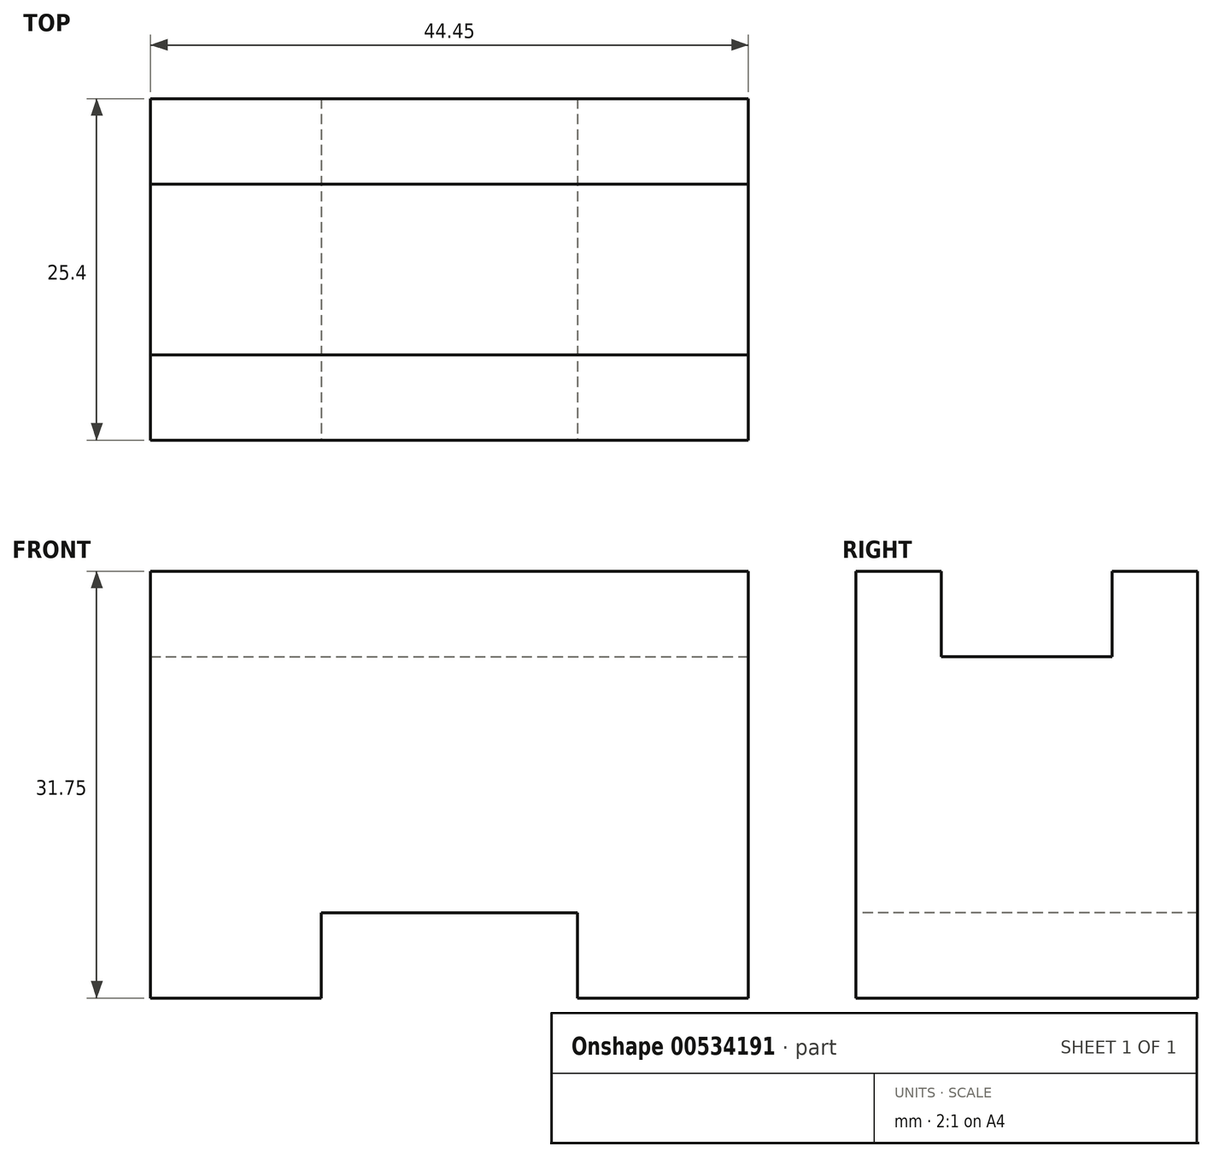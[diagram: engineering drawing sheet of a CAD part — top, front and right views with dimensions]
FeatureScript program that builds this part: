
annotation { "Feature Type Name" : "Feature", "Feature Type Description" : "" }
export const myFeature = defineFeature(function(context is Context, id is Id, definition is map)
    precondition{}
    {
        {
            var Q0;
            Q0=qCreatedBy(makeId("Right.planeOp"),FACE);
            var sketch = newSketch(context, id + "F0", { "sketchPlane" : qUnion([Q0])});
            skLineSegment(sketch, "E0", {"start": v(0, 0) * mm, "end": v(-25.4, 0) * mm});
            skLineSegment(sketch, "E1", {"start": v(0, 0) * mm, "end": v(0, 31.75) * mm});
            skLineSegment(sketch, "E2", {"start": v(0, 31.75) * mm, "end": v(-25.4, 31.75) * mm});
            skLineSegment(sketch, "E3", {"start": v(-25.4, 31.75) * mm, "end": v(-25.4, 0) * mm});
            skSolve(sketch);
        }
        {
            var Q0;
            Q0=makeQuery(id+"F0.imprint","IMPRINT",FACE,{"disambiguationData":[TD([[makeQuery(id+"F0.imprint","IMPRINT",EDGE,{"derivedFrom":sQuery(id+"F0.wireOp",EDGE,"E0")}),-1.0]])]});
            extrude(context, id + "F1", {"entities" : qUnion([Q0]), "oppositeDirection" : true, "depth" : 44.45 * mm, "offsetDistance" : 25.4 * mm});
        }
        {
            var Q0;
            Q0=makeQuery(id+"F1.opExtrude","SWEPT_FACE",FACE,{"disambiguationData":[OSD([sQuery(id+"F0.wireOp",EDGE,"E2")])]});
            var sketch = newSketch(context, id + "F2", { "sketchPlane" : qUnion([Q0])});
            skLineSegment(sketch, "E4", {"start": v(-44.45, -6.35) * mm, "end": v(0, -6.35) * mm});
            skLineSegment(sketch, "E5", {"start": v(-44.45, -19.05) * mm, "end": v(0, -19.05) * mm});
            skSolve(sketch);
        }
        {
            var Q0;
            {var subQ0=sQuery(id+"F2.wireOp",EDGE,"E4");Q0=makeQuery(id+"F2.imprint","IMPRINT",FACE,{"disambiguationData":[TD([[makeQuery(id+"F2.imprint","IMPRINT",EDGE,{"derivedFrom":subQ0}),-1.0]])]});}
            extrude(context, id + "F3", {"entities" : qUnion([Q0]), "operationType" : NewBodyOperationType.REMOVE, "oppositeDirection" : true, "depth" : 6.35 * mm, "offsetDistance" : 25.4 * mm});
        }
        {
            var Q0;
            Q0=makeQuery(id+"F1.opExtrude","SWEPT_FACE",FACE,{"disambiguationData":[OSD([sQuery(id+"F0.wireOp",EDGE,"E3")])]});
            var sketch = newSketch(context, id + "F4", { "sketchPlane" : qUnion([Q0])});
            skLineSegment(sketch, "E6", {"start": v(-31.75, 0) * mm, "end": v(-31.75, 6.35) * mm});
            skLineSegment(sketch, "E7", {"start": v(-31.75, 6.35) * mm, "end": v(-12.7, 6.35) * mm});
            skLineSegment(sketch, "E8", {"start": v(-12.7, 6.35) * mm, "end": v(-12.7, 0) * mm});
            skSolve(sketch);
        }
        {
            var Q0;
            {var subQ0=sQuery(id+"F4.wireOp",EDGE,"E6");Q0=makeQuery(id+"F4.imprint","IMPRINT",FACE,{"disambiguationData":[TD([[makeQuery(id+"F4.imprint","IMPRINT",EDGE,{"derivedFrom":subQ0}),-1.0]])]});}
            extrude(context, id + "F5", {"entities" : qUnion([Q0]), "operationType" : NewBodyOperationType.REMOVE, "oppositeDirection" : true, "depth" : 25.4 * mm, "offsetDistance" : 25.4 * mm});
        }
    });
